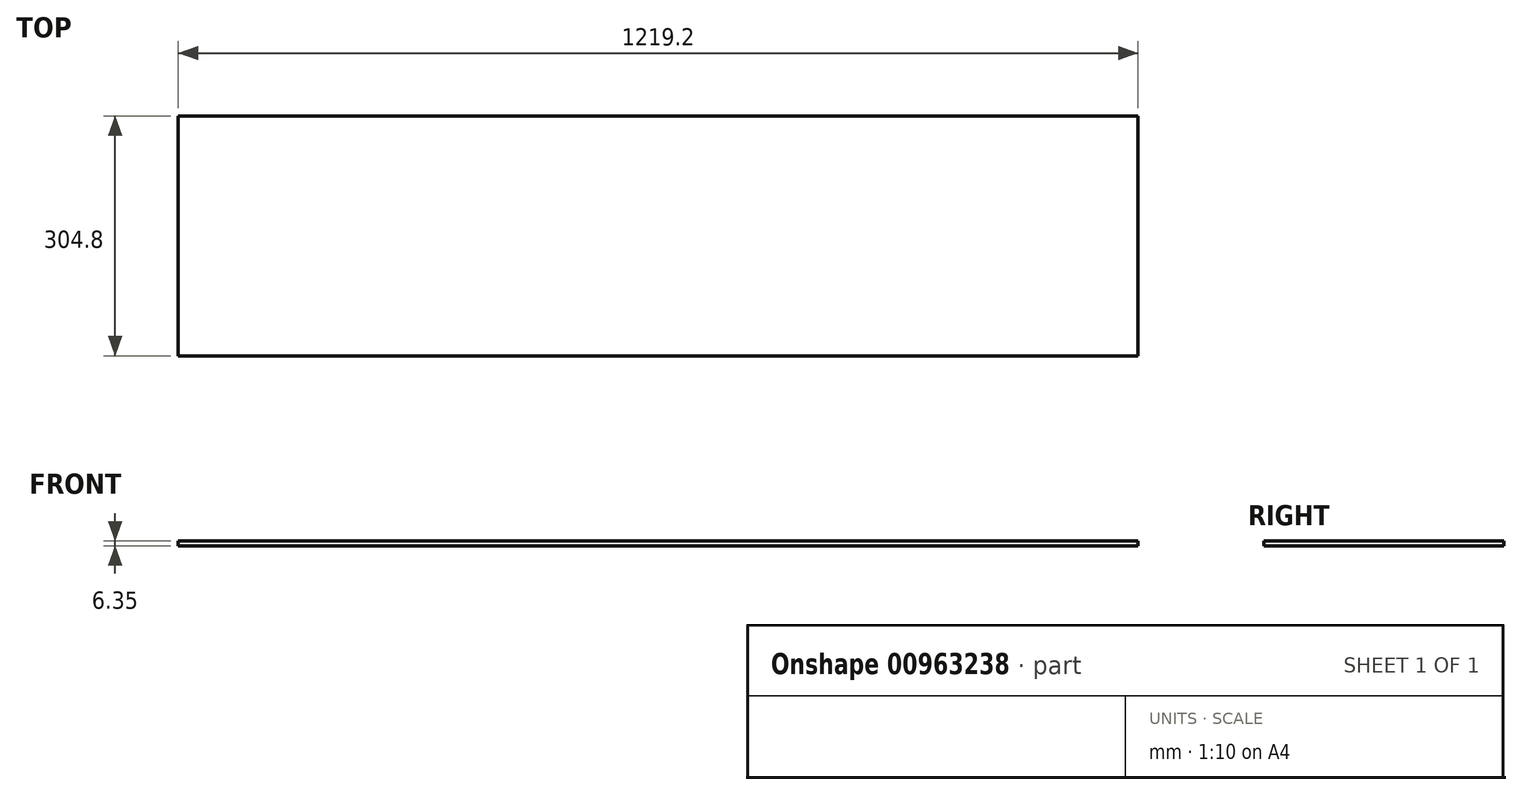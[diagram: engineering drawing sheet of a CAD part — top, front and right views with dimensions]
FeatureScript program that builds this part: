
annotation { "Feature Type Name" : "Feature", "Feature Type Description" : "" }
export const myFeature = defineFeature(function(context is Context, id is Id, definition is map)
    precondition{}
    {
        {
            var Q0;
            Q0=qCreatedBy(makeId("Top.planeOp"),FACE);
            var sketch = newSketch(context, id + "F0", { "sketchPlane" : qUnion([Q0])});
            skLineSegment(sketch, "E0.bottom", {"start": v(0, 0) * mm, "end": v(1219.2, 0) * mm});
            skLineSegment(sketch, "E0.top", {"start": v(0, 304.8) * mm, "end": v(1219.2, 304.8) * mm});
            skLineSegment(sketch, "E0.left", {"start": v(0, 0) * mm, "end": v(0, 304.8) * mm});
            skLineSegment(sketch, "E0.right", {"start": v(1219.2, 0) * mm, "end": v(1219.2, 304.8) * mm});
            skSolve(sketch);
        }
        {
            var Q0;
            Q0=makeQuery(id+"F0.imprint","IMPRINT",FACE,{"disambiguationData":[TD([[makeQuery(id+"F0.imprint","IMPRINT",EDGE,{"derivedFrom":sQuery(id+"F0.wireOp",EDGE,"E0.bottom")}),1.0]])]});
            extrude(context, id + "F1", {"entities" : qUnion([Q0]), "depth" : 6.35 * mm, "offsetDistance" : 25.4 * mm});
        }
    });
